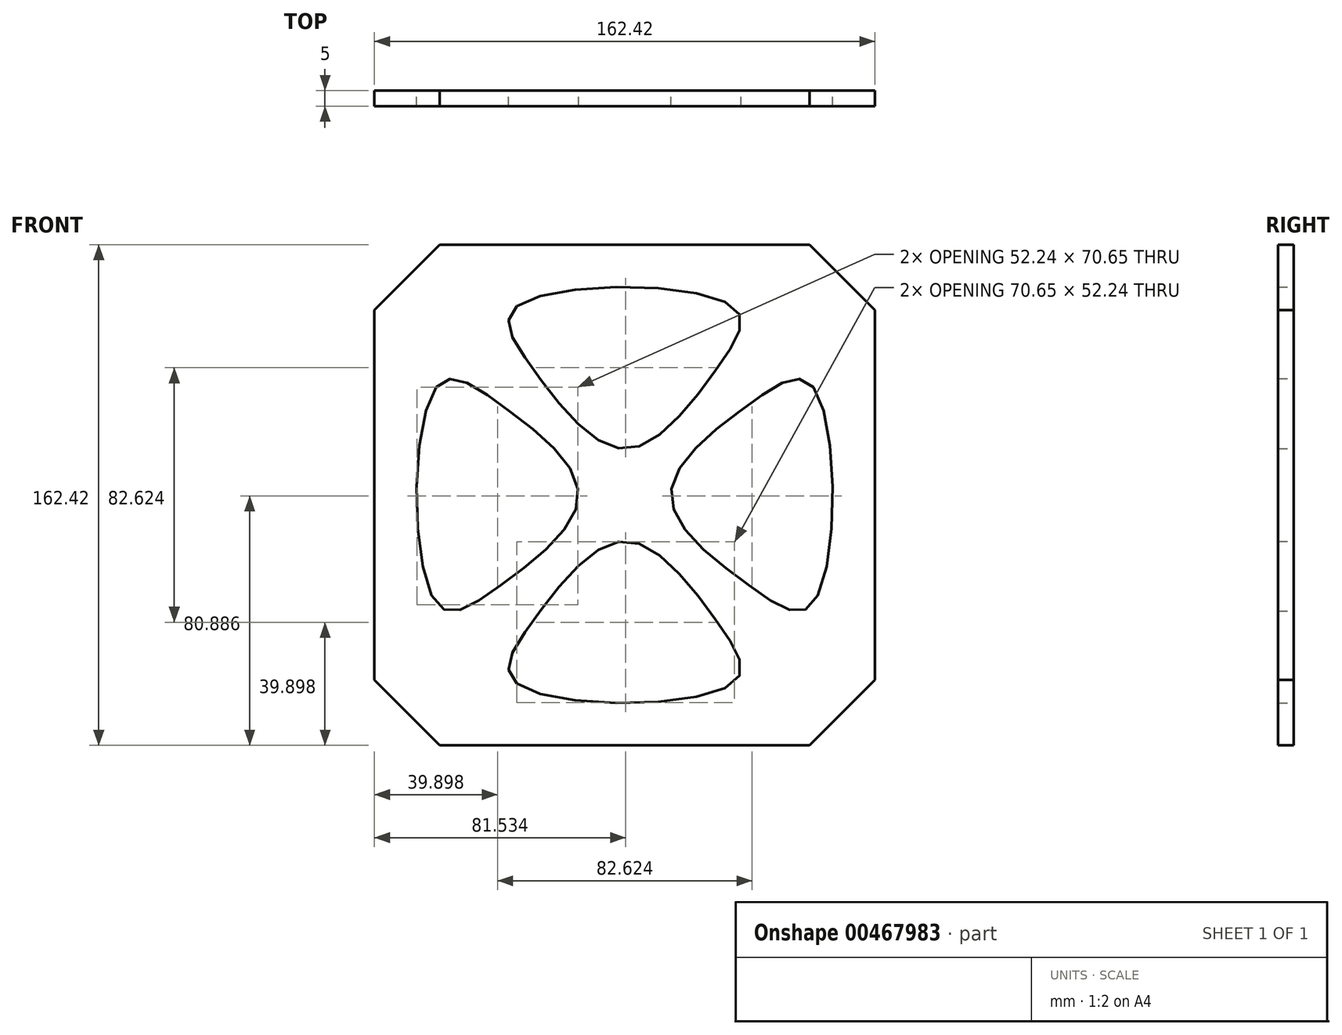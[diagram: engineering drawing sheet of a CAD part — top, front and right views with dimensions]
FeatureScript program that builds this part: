
annotation { "Feature Type Name" : "Feature", "Feature Type Description" : "" }
export const myFeature = defineFeature(function(context is Context, id is Id, definition is map)
    precondition{}
    {
        {
            var Q0;
            Q0=qCreatedBy(makeId("Front.planeOp"),FACE);
            var sketch = newSketch(context, id + "F0", { "sketchPlane" : qUnion([Q0])});
            skLineSegment(sketch, "E0", {"start": v(-81.21, 60) * mm, "end": v(-81.21, -60) * mm});
            skLineSegment(sketch, "E1", {"start": v(-81.21, -60) * mm, "end": v(-60, -81.21) * mm});
            skLineSegment(sketch, "E2", {"start": v(-60, -81.21) * mm, "end": v(60, -81.21) * mm});
            skLineSegment(sketch, "E3", {"start": v(60, -81.21) * mm, "end": v(81.21, -60) * mm});
            skLineSegment(sketch, "E4", {"start": v(81.21, -60) * mm, "end": v(81.21, 60) * mm});
            skLineSegment(sketch, "E5", {"start": v(81.21, 60) * mm, "end": v(60, 81.21) * mm});
            skLineSegment(sketch, "E6", {"start": v(60, 81.21) * mm, "end": v(-60, 81.21) * mm});
            skLineSegment(sketch, "E7", {"start": v(-60, 81.21) * mm, "end": v(-81.21, 60) * mm});
            skLineSegment(sketch, "E8", {"start": v(-61.21, 57.86) * mm, "end": v(-61.21, -56.85) * mm, "construction": true});
            skFitSpline(sketch, "E9", {"points": [v(-61.21, 35) * mm, v(-41.21, 30) * mm, v(-15, 0) * mm, v(-41.21, -30) * mm, v(-61.21, -35) * mm, v(-61.21, 35) * mm]});
            skLineSegment(sketch, "E10", {"start": v(0, 0) * mm, "end": v(-83.2, 83.2) * mm, "construction": true});
            skLineSegment(sketch, "E11", {"start": v(-41.21, 66.62) * mm, "end": v(-41.21, -51.55) * mm, "construction": true});
            skFitSpline(sketch, "E12.MirrorC", {"points": [v(61.21, 35) * mm, v(41.21, 30) * mm, v(15, 0) * mm, v(41.21, -30) * mm, v(61.21, -35) * mm, v(61.21, 35) * mm]});
            skFitSpline(sketch, "E13.MirrorC", {"points": [v(-35, 61.21) * mm, v(-30, 41.21) * mm, v(0, 15) * mm, v(30, 41.21) * mm, v(35, 61.21) * mm, v(-35, 61.21) * mm]});
            skFitSpline(sketch, "E14.MirrorC", {"points": [v(-35, -61.21) * mm, v(-30, -41.21) * mm, v(0, -15) * mm, v(30, -41.21) * mm, v(35, -61.21) * mm, v(-35, -61.21) * mm]});
            skSolve(sketch);
        }
        {
            var Q0;
            Q0 = qSketchRegion(id + "F0", true);
            extrude(context, id + "F1", {"entities" : qUnion([Q0]), "depth" : 5 * mm});
        }
    });
